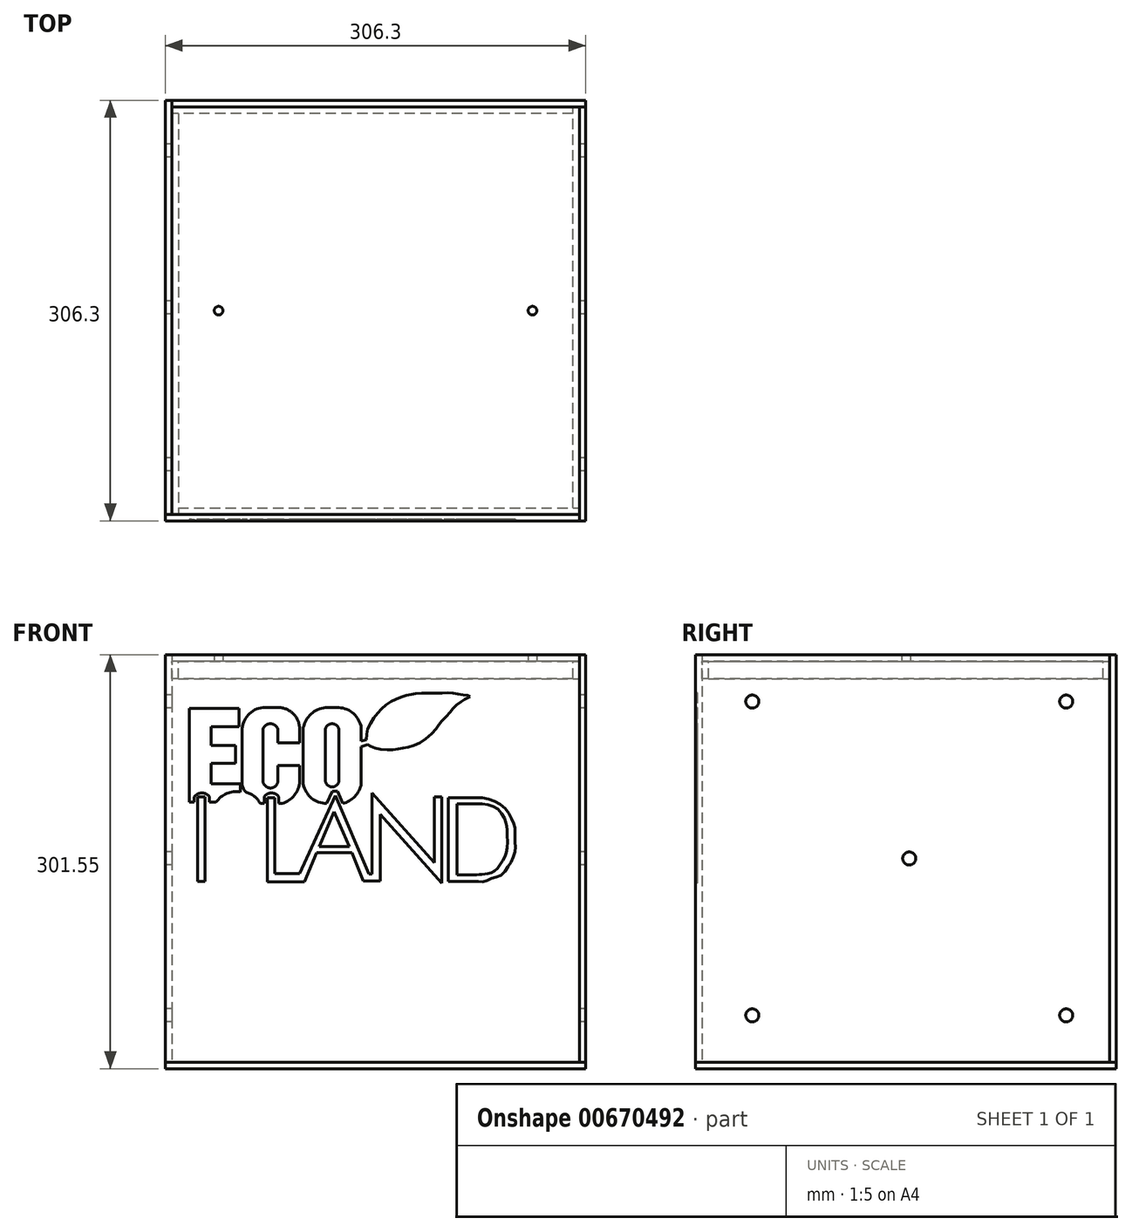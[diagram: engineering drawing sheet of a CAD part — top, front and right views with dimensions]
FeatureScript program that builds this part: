
annotation { "Feature Type Name" : "Feature", "Feature Type Description" : "" }
export const myFeature = defineFeature(function(context is Context, id is Id, definition is map)
    precondition{}
    {
        {
            var Q0;
            Q0=qCreatedBy(makeId("Top.planeOp"),FACE);
            var sketch = newSketch(context, id + "F0", { "sketchPlane" : qUnion([Q0])});
            skLineSegment(sketch, "E0.bottom", {"start": v(-148.4, -148.4) * mm, "end": v(148.4, -148.4) * mm});
            skLineSegment(sketch, "E0.top", {"start": v(-148.4, 148.4) * mm, "end": v(148.4, 148.4) * mm});
            skLineSegment(sketch, "E0.left", {"start": v(-148.4, -148.4) * mm, "end": v(-148.4, 148.4) * mm});
            skLineSegment(sketch, "E0.right", {"start": v(148.4, -148.4) * mm, "end": v(148.4, 148.4) * mm});
            skLineSegment(sketch, "E1.0", {"start": v(-153.15, 153.15) * mm, "end": v(153.15, 153.15) * mm});
            skLineSegment(sketch, "E1.1", {"start": v(-153.15, -153.15) * mm, "end": v(-153.15, 153.15) * mm});
            skLineSegment(sketch, "E1.2", {"start": v(-153.15, -153.15) * mm, "end": v(153.15, -153.15) * mm});
            skLineSegment(sketch, "E1.3", {"start": v(153.15, -153.15) * mm, "end": v(153.15, 153.15) * mm});
            skLineSegment(sketch, "E2", {"start": v(-148.4, 148.4) * mm, "end": v(-148.4, 153.15) * mm});
            skLineSegment(sketch, "E3", {"start": v(-148.4, -148.4) * mm, "end": v(-153.15, -148.4) * mm});
            skLineSegment(sketch, "E4", {"start": v(148.4, -148.4) * mm, "end": v(148.4, -153.15) * mm});
            skLineSegment(sketch, "E5", {"start": v(148.4, 148.4) * mm, "end": v(153.15, 148.4) * mm});
            skSolve(sketch);
        }
        {
            var Q0;
            Q0=makeQuery(id+"F0.imprint","IMPRINT",FACE,{"disambiguationData":[TD([[makeQuery(id+"F0.imprint","IMPRINT",EDGE,{"derivedFrom":sQuery(id+"F0.wireOp",EDGE,"E0.top")}),1.0]])]});
            extrude(context, id + "F1", {"entities" : qUnion([Q0]), "depth" : 296.8 * mm, "offsetDistance" : 25.4 * mm});
        }
        {
            var Q0;
            Q0=makeQuery(id+"F0.imprint","IMPRINT",FACE,{"disambiguationData":[TD([[makeQuery(id+"F0.imprint","IMPRINT",EDGE,{"derivedFrom":sQuery(id+"F0.wireOp",EDGE,"E0.left")}),1.0]])]});
            extrude(context, id + "F2", {"entities" : qUnion([Q0]), "depth" : 296.8 * mm, "offsetDistance" : 25.4 * mm});
        }
        {
            var Q0;
            Q0=makeQuery(id+"F0.imprint","IMPRINT",FACE,{"disambiguationData":[TD([[makeQuery(id+"F0.imprint","IMPRINT",EDGE,{"derivedFrom":sQuery(id+"F0.wireOp",EDGE,"E0.bottom")}),-1.0]])]});
            extrude(context, id + "F3", {"entities" : qUnion([Q0]), "depth" : 296.8 * mm, "offsetDistance" : 25.4 * mm});
        }
        {
            var Q0;
            Q0=makeQuery(id+"F0.imprint","IMPRINT",FACE,{"disambiguationData":[TD([[makeQuery(id+"F0.imprint","IMPRINT",EDGE,{"derivedFrom":sQuery(id+"F0.wireOp",EDGE,"E0.right")}),-1.0]])]});
            extrude(context, id + "F4", {"entities" : qUnion([Q0]), "depth" : 296.8 * mm, "offsetDistance" : 25.4 * mm});
        }
        {
            var Q0;
            Q0=makeQuery(id+"F0.imprint","IMPRINT",FACE,{"disambiguationData":[TD([[makeQuery(id+"F0.imprint","IMPRINT",EDGE,{"derivedFrom":sQuery(id+"F0.wireOp",EDGE,"E0.bottom")}),1.0]])]});
            var Q1;
            Q1=makeQuery(id+"F0.imprint","IMPRINT",FACE,{"disambiguationData":[TD([[makeQuery(id+"F0.imprint","IMPRINT",EDGE,{"derivedFrom":sQuery(id+"F0.wireOp",EDGE,"E0.bottom")}),-1.0]])]});
            var Q2;
            Q2=makeQuery(id+"F0.imprint","IMPRINT",FACE,{"disambiguationData":[TD([[makeQuery(id+"F0.imprint","IMPRINT",EDGE,{"derivedFrom":sQuery(id+"F0.wireOp",EDGE,"E0.left")}),1.0]])]});
            var Q3;
            Q3=makeQuery(id+"F0.imprint","IMPRINT",FACE,{"disambiguationData":[TD([[makeQuery(id+"F0.imprint","IMPRINT",EDGE,{"derivedFrom":sQuery(id+"F0.wireOp",EDGE,"E0.right")}),-1.0]])]});
            var Q4;
            Q4=makeQuery(id+"F0.imprint","IMPRINT",FACE,{"disambiguationData":[TD([[makeQuery(id+"F0.imprint","IMPRINT",EDGE,{"derivedFrom":sQuery(id+"F0.wireOp",EDGE,"E0.top")}),1.0]])]});
            extrude(context, id + "F5", {"entities" : qUnion([Q0, Q1, Q2, Q3, Q4]), "oppositeDirection" : true, "depth" : 4.75 * mm, "offsetDistance" : 25.4 * mm});
        }
        {
            var Q0;
            Q0=makeQuery(id+"F2.opExtrude","CAP_FACE",FACE,{"disambiguationData":[OSD([sQuery(id+"F0.wireOp",EDGE,"E0.left"),sQuery(id+"F0.wireOp",EDGE,"E1.0"),sQuery(id+"F0.wireOp",EDGE,"E1.1"),sQuery(id+"F0.wireOp",EDGE,"E2"),sQuery(id+"F0.wireOp",EDGE,"E3")])],"isStart":false});
            cPlane(context, id + "F6", {"entities" : qUnion([Q0]), "cplaneType" : CPlaneType.OFFSET, "offset" : 4.75 * mm, "oppositeDirection" : true, "width" : 152.4 * mm, "height" : 152.4 * mm});
        }
        {
            var Q0;
            Q0=qCreatedBy(id+"F6.planeOp",FACE);
            var sketch = newSketch(context, id + "F7", { "sketchPlane" : qUnion([Q0])});
            skLineSegment(sketch, "E6.0.0", {"start": v(148.4, 148.4) * mm, "end": v(-148.4, 148.4) * mm});
            skLineSegment(sketch, "E6.0.1", {"start": v(-148.4, 148.4) * mm, "end": v(-148.4, -148.4) * mm});
            skLineSegment(sketch, "E6.0.2", {"start": v(-148.4, -148.4) * mm, "end": v(148.4, -148.4) * mm});
            skLineSegment(sketch, "E6.0.3", {"start": v(148.4, -148.4) * mm, "end": v(148.4, 148.4) * mm});
            skLineSegment(sketch, "E7.0", {"start": v(143.65, 143.65) * mm, "end": v(-143.65, 143.65) * mm});
            skLineSegment(sketch, "E7.1", {"start": v(143.65, -143.65) * mm, "end": v(143.65, 143.65) * mm});
            skLineSegment(sketch, "E7.2", {"start": v(-143.65, -143.65) * mm, "end": v(143.65, -143.65) * mm});
            skLineSegment(sketch, "E7.3", {"start": v(-143.65, 143.65) * mm, "end": v(-143.65, -143.65) * mm});
            skLineSegment(sketch, "E8", {"start": v(-143.65, 143.65) * mm, "end": v(-148.4, 143.65) * mm});
            skLineSegment(sketch, "E9", {"start": v(143.65, 143.65) * mm, "end": v(143.65, 148.4) * mm});
            skLineSegment(sketch, "E10", {"start": v(143.65, -143.65) * mm, "end": v(148.4, -143.65) * mm});
            skLineSegment(sketch, "E11", {"start": v(-143.65, -143.65) * mm, "end": v(-143.65, -148.4) * mm});
            skSolve(sketch);
        }
        {
            var Q0;
            Q0=makeQuery(id+"F7.imprint","IMPRINT",FACE,{"disambiguationData":[TD([[makeQuery(id+"F7.imprint","IMPRINT",EDGE,{"derivedFrom":sQuery(id+"F7.wireOp",EDGE,"E7.0")}),-1.0]])]});
            extrude(context, id + "F8", {"entities" : qUnion([Q0]), "oppositeDirection" : true, "depth" : 12.7 * mm, "offsetDistance" : 25.4 * mm});
        }
        {
            var Q0;
            Q0=makeQuery(id+"F7.imprint","IMPRINT",FACE,{"disambiguationData":[TD([[makeQuery(id+"F7.imprint","IMPRINT",EDGE,{"derivedFrom":sQuery(id+"F7.wireOp",EDGE,"E7.1")}),-1.0]])]});
            extrude(context, id + "F9", {"entities" : qUnion([Q0]), "oppositeDirection" : true, "depth" : 12.7 * mm, "offsetDistance" : 25.4 * mm});
        }
        {
            var Q0;
            Q0=makeQuery(id+"F7.imprint","IMPRINT",FACE,{"disambiguationData":[TD([[makeQuery(id+"F7.imprint","IMPRINT",EDGE,{"derivedFrom":sQuery(id+"F7.wireOp",EDGE,"E7.2")}),-1.0]])]});
            extrude(context, id + "F10", {"entities" : qUnion([Q0]), "oppositeDirection" : true, "depth" : 12.7 * mm, "offsetDistance" : 25.4 * mm});
        }
        {
            var Q0;
            Q0=makeQuery(id+"F7.imprint","IMPRINT",FACE,{"disambiguationData":[TD([[makeQuery(id+"F7.imprint","IMPRINT",EDGE,{"derivedFrom":sQuery(id+"F7.wireOp",EDGE,"E7.3")}),-1.0]])]});
            extrude(context, id + "F11", {"entities" : qUnion([Q0]), "oppositeDirection" : true, "depth" : 12.7 * mm, "offsetDistance" : 25.4 * mm});
        }
        {
            var Q0;
            Q0=qCreatedBy(id+"F6.planeOp",FACE);
            var sketch = newSketch(context, id + "F12", { "sketchPlane" : qUnion([Q0])});
            skLineSegment(sketch, "E12.0.0", {"start": v(148.4, 148.4) * mm, "end": v(-148.4, 148.4) * mm});
            skLineSegment(sketch, "E12.0.1", {"start": v(-148.4, 148.4) * mm, "end": v(-148.4, -148.4) * mm});
            skLineSegment(sketch, "E12.0.2", {"start": v(-148.4, -148.4) * mm, "end": v(148.4, -148.4) * mm});
            skLineSegment(sketch, "E12.0.3", {"start": v(148.4, -148.4) * mm, "end": v(148.4, 148.4) * mm});
            skCircle(sketch, "E13", {"center": v(-114.3, 0) * mm, "radius": 3.18 * mm});
            skCircle(sketch, "E14", {"center": v(114.3, 0) * mm, "radius": 3.18 * mm});
            skSolve(sketch);
        }
        {
            var Q0;
            Q0=makeQuery(id+"F12.imprint","IMPRINT",FACE,{"disambiguationData":[TD([[makeQuery(id+"F12.imprint","IMPRINT",EDGE,{"derivedFrom":sQuery(id+"F12.wireOp",EDGE,"E12.0.0")}),1.0]])]});
            extrude(context, id + "F13", {"entities" : qUnion([Q0]), "depth" : 4.75 * mm, "offsetDistance" : 25.4 * mm});
        }
        {
            var Q0;
            Q0=makeQuery(id+"F2.opExtrude","SWEPT_FACE",FACE,{"disambiguationData":[OSD([sQuery(id+"F0.wireOp",EDGE,"E1.1")])]});
            var sketch = newSketch(context, id + "F14", { "sketchPlane" : qUnion([Q0])});
            skCircle(sketch, "E15", {"center": v(-116.67, 262.7) * mm, "radius": 4.76 * mm});
            skCircle(sketch, "E16", {"center": v(111.93, 262.7) * mm, "radius": 4.76 * mm});
            skCircle(sketch, "E17", {"center": v(-2.37, 148.4) * mm, "radius": 4.76 * mm});
            skCircle(sketch, "E18", {"center": v(-116.67, 34.1) * mm, "radius": 4.76 * mm});
            skCircle(sketch, "E19", {"center": v(111.93, 34.1) * mm, "radius": 4.76 * mm});
            skLineSegment(sketch, "E20", {"start": v(-2.37, 296.8) * mm, "end": v(-2.37, -5.46) * mm, "construction": true});
            skPoint(sketch, "E21.endSnap0", {"position": v(-153.15, 148.4) * mm});
            skLineSegment(sketch, "E22", {"start": v(-153.15, 148.4) * mm, "end": v(153.15, 148.4) * mm, "construction": true});
            skPoint(sketch, "E22.endSnap0", {"position": v(148.4, 148.4) * mm});
            skLineSegment(sketch, "E23.0", {"start": v(-153.15, 262.7) * mm, "end": v(153.15, 262.7) * mm, "construction": true});
            skLineSegment(sketch, "E24.MirrorCS", {"start": v(-153.15, 34.1) * mm, "end": v(153.15, 34.1) * mm, "construction": true});
            skLineSegment(sketch, "E25.0", {"start": v(-116.67, 309.55) * mm, "end": v(-116.67, -5.46) * mm, "construction": true});
            skLineSegment(sketch, "E26.MirrorCS", {"start": v(111.93, 309.55) * mm, "end": v(111.93, -5.46) * mm, "construction": true});
            skSolve(sketch);
        }
        {
            var Q0;
            Q0=makeQuery(id+"F14.imprint","IMPRINT",FACE,{"disambiguationData":[TD([[makeQuery(id+"F14.imprint","IMPRINT",EDGE,{"derivedFrom":sQuery(id+"F14.wireOp",EDGE,"E15")}),1.0]])]});
            var Q1;
            Q1=makeQuery(id+"F14.imprint","IMPRINT",FACE,{"disambiguationData":[TD([[makeQuery(id+"F14.imprint","IMPRINT",EDGE,{"derivedFrom":sQuery(id+"F14.wireOp",EDGE,"E17")}),1.0]])]});
            var Q2;
            Q2=makeQuery(id+"F14.imprint","IMPRINT",FACE,{"disambiguationData":[TD([[makeQuery(id+"F14.imprint","IMPRINT",EDGE,{"derivedFrom":sQuery(id+"F14.wireOp",EDGE,"E16")}),1.0]])]});
            var Q3;
            Q3=makeQuery(id+"F14.imprint","IMPRINT",FACE,{"disambiguationData":[TD([[makeQuery(id+"F14.imprint","IMPRINT",EDGE,{"derivedFrom":sQuery(id+"F14.wireOp",EDGE,"E18")}),1.0]])]});
            var Q4;
            Q4=makeQuery(id+"F14.imprint","IMPRINT",FACE,{"disambiguationData":[TD([[makeQuery(id+"F14.imprint","IMPRINT",EDGE,{"derivedFrom":sQuery(id+"F14.wireOp",EDGE,"E19")}),1.0]])]});
            extrude(context, id + "F15", {"entities" : qUnion([Q0, Q1, Q2, Q3, Q4]), "operationType" : NewBodyOperationType.REMOVE, "endBound" : BoundingType.THROUGH_ALL, "oppositeDirection" : true, "depth" : 25.4 * mm, "offsetDistance" : 25.4 * mm});
        }
        {
            var Q0;
            Q0=makeQuery(id+"F3.opExtrude","SWEPT_FACE",FACE,{"disambiguationData":[OSD([sQuery(id+"F0.wireOp",EDGE,"E1.2")])]});
            var sketch = newSketch(context, id + "F16", { "sketchPlane" : qUnion([Q0])});
            skArc(sketch, "E27", {"start": v(-8.6, 125.15) * mm, "mid": v(-10.23, 126.38) * mm, "end": v(-11.85, 125.15) * mm});
            skLineSegment(sketch, "E28", {"start": v(-8.6, 125.15) * mm, "end": v(-8.6, 112.33) * mm});
            skArc(sketch, "E29", {"start": v(-11.85, 112.33) * mm, "mid": v(-10.23, 111.03) * mm, "end": v(-8.6, 112.33) * mm});
            skLineSegment(sketch, "E30", {"start": v(-11.85, 112.33) * mm, "end": v(-11.85, 125.15) * mm});
            skArc(sketch, "E31", {"start": v(-11.85, 130.29) * mm, "mid": v(-15.35, 128.72) * mm, "end": v(-17.23, 125.38) * mm});
            skLineSegment(sketch, "E32", {"start": v(-8.6, 130.29) * mm, "end": v(-11.85, 130.29) * mm});
            skArc(sketch, "E33", {"start": v(-3.14, 125.38) * mm, "mid": v(-5.01, 128.8) * mm, "end": v(-8.6, 130.29) * mm});
            skLineSegment(sketch, "E34", {"start": v(-3.14, 122.14) * mm, "end": v(-3.14, 125.38) * mm});
            skLineSegment(sketch, "E35", {"start": v(-1.95, 122.5) * mm, "end": v(-3.14, 122.14) * mm});
            skFitSpline(sketch, "E36", {"points": [v(23.25, 132.99) * mm, v(22.72, 133.21) * mm, v(21.03, 133.46) * mm, v(19.07, 133.84) * mm, v(16.72, 133.84) * mm, v(13.07, 133.84) * mm, v(9.94, 133.63) * mm, v(8.25, 133.32) * mm, v(6.05, 132.64) * mm, v(3.77, 131.57) * mm, v(1.55, 129.79) * mm, v(-0.23, 127.6) * mm, v(-1.66, 124.84) * mm, v(-1.95, 122.5) * mm]});
            skFitSpline(sketch, "E37", {"points": [v(-1.57, 121.3) * mm, v(-0.72, 120.85) * mm, v(1.44, 120.18) * mm, v(4.5, 120.06) * mm, v(6.42, 120.36) * mm, v(8.83, 120.8) * mm, v(11.86, 122.23) * mm, v(15.02, 125.15) * mm, v(16, 126.51) * mm, v(17.9, 128.59) * mm, v(19.23, 130.21) * mm, v(20.94, 131.57) * mm, v(22.39, 132.49) * mm, v(23.07, 132.86) * mm, v(23.25, 132.99) * mm]});
            skLineSegment(sketch, "E38", {"start": v(-3.14, 120.8) * mm, "end": v(-1.57, 121.3) * mm});
            skLineSegment(sketch, "E39", {"start": v(-3.14, 111.76) * mm, "end": v(-3.14, 120.8) * mm});
            skArc(sketch, "E40", {"start": v(-7.69, 107) * mm, "mid": v(-4.71, 108.7) * mm, "end": v(-3.14, 111.76) * mm});
            skLineSegment(sketch, "E41", {"start": v(-8.94, 110.02) * mm, "end": v(-7.69, 107) * mm});
            skLineSegment(sketch, "E42", {"start": v(-10.23, 110.02) * mm, "end": v(-8.94, 110.02) * mm});
            skLineSegment(sketch, "E43", {"start": v(-11.52, 107) * mm, "end": v(-10.23, 110.02) * mm});
            skArc(sketch, "E44", {"start": v(-17.23, 111.76) * mm, "mid": v(-15.25, 108.32) * mm, "end": v(-11.52, 107) * mm});
            skLineSegment(sketch, "E45", {"start": v(-17.23, 125.38) * mm, "end": v(-17.23, 111.76) * mm});
            skFitSpline(sketch, "E46", {"points": [v(26.21, 106.92) * mm, v(30.03, 105.58) * mm, v(31.97, 102.38) * mm, v(32.23, 100.6) * mm, v(32.23, 96) * mm, v(31.5, 93.66) * mm, v(29.77, 91.13) * mm, v(28.35, 90.2) * mm, v(26.9, 89.88) * mm, v(25.75, 89.77) * mm, v(24.83, 89.7) * mm]});
            skLineSegment(sketch, "E47", {"start": v(24.83, 89.7) * mm, "end": v(20.09, 89.7) * mm});
            skLineSegment(sketch, "E48", {"start": v(20.09, 89.7) * mm, "end": v(20.09, 106.92) * mm});
            skLineSegment(sketch, "E49", {"start": v(20.09, 106.92) * mm, "end": v(26.21, 106.92) * mm});
            skLineSegment(sketch, "E50", {"start": v(26.2, 108.36) * mm, "end": v(18.02, 108.36) * mm});
            skFitSpline(sketch, "E51", {"points": [v(25.26, 88.07) * mm, v(26.9, 88.07) * mm, v(28.65, 88.87) * mm, v(30.52, 89.42) * mm, v(32.23, 91.3) * mm, v(33.5, 93.37) * mm, v(34.2, 95.62) * mm, v(34.2, 97.62) * mm, v(34.2, 100.15) * mm, v(34.2, 101.2) * mm, v(33.45, 102.97) * mm, v(32.11, 105.38) * mm, v(29.35, 107.47) * mm, v(26.2, 108.36) * mm]});
            skLineSegment(sketch, "E52", {"start": v(18.02, 88.07) * mm, "end": v(25.26, 88.07) * mm});
            skLineSegment(sketch, "E53", {"start": v(18.02, 108.36) * mm, "end": v(18.02, 88.07) * mm});
            skLineSegment(sketch, "E54", {"start": v(-32.88, 130.05) * mm, "end": v(-44.89, 130.05) * mm});
            skLineSegment(sketch, "E55", {"start": v(-32.88, 125.6) * mm, "end": v(-32.88, 130.05) * mm});
            skLineSegment(sketch, "E56", {"start": v(-39.55, 125.6) * mm, "end": v(-32.88, 125.6) * mm});
            skLineSegment(sketch, "E57", {"start": v(-39.55, 121.07) * mm, "end": v(-39.55, 125.6) * mm});
            skLineSegment(sketch, "E58", {"start": v(-33.63, 121.07) * mm, "end": v(-39.55, 121.07) * mm});
            skLineSegment(sketch, "E59", {"start": v(-33.63, 116.75) * mm, "end": v(-33.63, 121.07) * mm});
            skLineSegment(sketch, "E60", {"start": v(-39.55, 116.75) * mm, "end": v(-33.63, 116.75) * mm});
            skLineSegment(sketch, "E61", {"start": v(-39.55, 111.76) * mm, "end": v(-39.55, 116.75) * mm});
            skLineSegment(sketch, "E62", {"start": v(-32.5, 111.76) * mm, "end": v(-39.55, 111.76) * mm});
            skLineSegment(sketch, "E63", {"start": v(-32.5, 109.78) * mm, "end": v(-32.5, 111.76) * mm});
            skArc(sketch, "E64", {"start": v(-32.5, 109.78) * mm, "mid": v(-35.8, 109.4) * mm, "end": v(-38.4, 107.34) * mm});
            skLineSegment(sketch, "E65", {"start": v(-39.99, 107.34) * mm, "end": v(-38.4, 107.34) * mm});
            skLineSegment(sketch, "E66", {"start": v(-39.99, 108.6) * mm, "end": v(-39.99, 107.34) * mm});
            skArc(sketch, "E67", {"start": v(-39.99, 108.6) * mm, "mid": v(-41.84, 109.55) * mm, "end": v(-43.7, 108.6) * mm});
            skLineSegment(sketch, "E68", {"start": v(-43.7, 107.34) * mm, "end": v(-43.7, 108.6) * mm});
            skLineSegment(sketch, "E69", {"start": v(-44.89, 107.34) * mm, "end": v(-43.7, 107.34) * mm});
            skLineSegment(sketch, "E70", {"start": v(-44.89, 130.05) * mm, "end": v(-44.89, 107.34) * mm});
            skLineSegment(sketch, "E71", {"start": v(-9.73, 105) * mm, "end": v(-6.08, 96.57) * mm});
            skLineSegment(sketch, "E72", {"start": v(-6.08, 96.57) * mm, "end": v(-13.34, 96.57) * mm});
            skLineSegment(sketch, "E73", {"start": v(-13.34, 96.57) * mm, "end": v(-9.73, 105) * mm});
            skLineSegment(sketch, "E74", {"start": v(-24.14, 89.97) * mm, "end": v(-24.14, 108.36) * mm});
            skLineSegment(sketch, "E75", {"start": v(-18.16, 89.97) * mm, "end": v(-24.14, 89.97) * mm});
            skLineSegment(sketch, "E76", {"start": v(-9.45, 108.96) * mm, "end": v(-18.16, 89.97) * mm});
            skLineSegment(sketch, "E77", {"start": v(-1.29, 89.88) * mm, "end": v(-9.45, 108.96) * mm});
            skLineSegment(sketch, "E78", {"start": v(-2.71, 88.13) * mm, "end": v(-0.51, 88.13) * mm});
            skLineSegment(sketch, "E79", {"start": v(-5.47, 95.03) * mm, "end": v(-2.71, 88.13) * mm});
            skLineSegment(sketch, "E80", {"start": v(-14, 95.03) * mm, "end": v(-5.47, 95.03) * mm});
            skLineSegment(sketch, "E81", {"start": v(-17, 88.02) * mm, "end": v(-14, 95.03) * mm});
            skLineSegment(sketch, "E82", {"start": v(-25.93, 88.02) * mm, "end": v(-17, 88.02) * mm});
            skLineSegment(sketch, "E83", {"start": v(-25.93, 108.36) * mm, "end": v(-25.93, 88.02) * mm});
            skLineSegment(sketch, "E84", {"start": v(-24.14, 108.36) * mm, "end": v(-25.93, 108.36) * mm});
            skLineSegment(sketch, "E85", {"start": v(-0.51, 109.55) * mm, "end": v(-0.51, 89.88) * mm});
            skLineSegment(sketch, "E86", {"start": v(14.56, 92.6) * mm, "end": v(-0.51, 109.55) * mm});
            skLineSegment(sketch, "E87", {"start": v(14.56, 108.6) * mm, "end": v(14.56, 92.6) * mm});
            skLineSegment(sketch, "E88", {"start": v(16.34, 108.6) * mm, "end": v(14.56, 108.6) * mm});
            skLineSegment(sketch, "E89", {"start": v(16.34, 87.62) * mm, "end": v(16.34, 108.6) * mm});
            skLineSegment(sketch, "E90", {"start": v(1.44, 104.38) * mm, "end": v(16.34, 87.62) * mm});
            skLineSegment(sketch, "E91", {"start": v(1.44, 88.02) * mm, "end": v(1.44, 104.38) * mm});
            skLineSegment(sketch, "E92", {"start": v(-0.51, 88.13) * mm, "end": v(1.45, 88.13) * mm});
            skFitSpline(sketch, "E93", {"points": [v(-39.55, 91.54) * mm, v(-39.2, 90.9) * mm, v(-38.58, 89.97) * mm, v(-37.66, 88.87) * mm, v(-36.07, 88.02) * mm, v(-34.9, 87.63) * mm, v(-32.5, 87.63) * mm, v(-32.5, 87.63) * mm, v(-31.22, 87.9) * mm, v(-29.93, 88.35) * mm, v(-28.75, 89.47) * mm, v(-27.9, 90.5) * mm, v(-27.3, 91.92) * mm, v(-27.3, 93.66) * mm, v(-27.57, 95.15) * mm, v(-28.06, 96.57) * mm, v(-29.42, 97.98) * mm, v(-31.29, 99.33) * mm, v(-32.88, 100.15) * mm, v(-34.4, 100.92) * mm, v(-35.8, 102.21) * mm, v(-36.4, 102.87) * mm, v(-36.59, 103.98) * mm, v(-36.55, 105.37) * mm, v(-36.4, 105.91) * mm, v(-35.7, 106.64) * mm, v(-34.9, 107.1) * mm, v(-34.29, 107.44) * mm, v(-33.22, 107.44) * mm, v(-32.37, 107.44) * mm, v(-31.83, 107.22) * mm, v(-30.85, 106.78) * mm, v(-29.72, 105.55) * mm]});
            skLineSegment(sketch, "E94", {"start": v(-38.07, 92.49) * mm, "end": v(-39.55, 91.54) * mm});
            skFitSpline(sketch, "E95", {"points": [v(-28.36, 106.37) * mm, v(-29.87, 108.07) * mm, v(-30.97, 108.64) * mm, v(-32.1, 108.86) * mm, v(-33.44, 108.96) * mm, v(-34.87, 108.8) * mm, v(-36.18, 108.26) * mm, v(-36.9, 107.68) * mm, v(-37.68, 107) * mm, v(-38.2, 105.96) * mm, v(-38.5, 105.24) * mm, v(-38.61, 104.37) * mm, v(-38.52, 102.97) * mm, v(-38.11, 101.8) * mm, v(-37.34, 101.08) * mm, v(-35.38, 99.55) * mm, v(-33.13, 98.33) * mm, v(-31.29, 97.13) * mm, v(-29.93, 96.01) * mm, v(-29.35, 94.95) * mm, v(-29.09, 93.5) * mm, v(-29.09, 92.32) * mm, v(-29.61, 91.08) * mm, v(-30.62, 90) * mm, v(-31.67, 89.43) * mm, v(-32.5, 89.21) * mm, v(-33.7, 89.21) * mm, v(-34.29, 89.21) * mm, v(-35.8, 89.73) * mm, v(-36.55, 90.2) * mm, v(-37.16, 90.97) * mm, v(-37.66, 91.68) * mm, v(-38.07, 92.49) * mm]});
            skLineSegment(sketch, "E96", {"start": v(-29.72, 105.55) * mm, "end": v(-28.36, 106.37) * mm});
            skLineSegment(sketch, "E97", {"start": v(-41.05, 88.06) * mm, "end": v(-41.05, 108.6) * mm});
            skLineSegment(sketch, "E98", {"start": v(-42.84, 88.06) * mm, "end": v(-41.05, 88.06) * mm});
            skLineSegment(sketch, "E99", {"start": v(-42.84, 108.6) * mm, "end": v(-42.84, 88.06) * mm});
            skLineSegment(sketch, "E100", {"start": v(-41.05, 108.6) * mm, "end": v(-42.84, 108.6) * mm});
            skLineSegment(sketch, "E101", {"start": v(51.59, 95.86) * mm, "end": v(51.59, 88.87) * mm});
            skLineSegment(sketch, "E102", {"start": v(52.13, 95.86) * mm, "end": v(51.59, 95.86) * mm});
            skLineSegment(sketch, "E103", {"start": v(52.13, 89.32) * mm, "end": v(52.13, 95.86) * mm});
            skLineSegment(sketch, "E104", {"start": v(54.69, 89.32) * mm, "end": v(52.13, 89.32) * mm});
            skLineSegment(sketch, "E105", {"start": v(54.69, 88.87) * mm, "end": v(54.69, 89.32) * mm});
            skLineSegment(sketch, "E106", {"start": v(51.59, 88.87) * mm, "end": v(54.69, 88.87) * mm});
            skLineSegment(sketch, "E107", {"start": v(48.62, 89.32) * mm, "end": v(48.62, 95.86) * mm});
            skLineSegment(sketch, "E108", {"start": v(51.18, 89.32) * mm, "end": v(48.62, 89.32) * mm});
            skLineSegment(sketch, "E109", {"start": v(51.18, 88.87) * mm, "end": v(51.18, 89.32) * mm});
            skLineSegment(sketch, "E110", {"start": v(48.08, 88.87) * mm, "end": v(51.18, 88.87) * mm});
            skLineSegment(sketch, "E111", {"start": v(48.08, 95.86) * mm, "end": v(48.08, 88.87) * mm});
            skLineSegment(sketch, "E112", {"start": v(48.62, 95.86) * mm, "end": v(48.08, 95.86) * mm});
            skLineSegment(sketch, "E113", {"start": v(61.15, 94.65) * mm, "end": v(61.15, 95.73) * mm});
            skArc(sketch, "E114", {"start": v(61.15, 94.65) * mm, "mid": v(55.43, 92.49) * mm, "end": v(61.15, 90.32) * mm});
            skLineSegment(sketch, "E115", {"start": v(61.15, 89.24) * mm, "end": v(61.15, 90.32) * mm});
            skArc(sketch, "E116", {"start": v(61.15, 95.73) * mm, "mid": v(54.63, 92.49) * mm, "end": v(61.15, 89.24) * mm});
            skFitSpline(sketch, "E117", {"points": [v(33.37, 91.54) * mm, v(33.72, 90.9) * mm, v(34.34, 89.97) * mm, v(35.26, 88.87) * mm, v(36.85, 88.02) * mm, v(38.02, 87.63) * mm, v(40.41, 87.63) * mm, v(40.41, 87.63) * mm, v(41.7, 87.9) * mm, v(43, 88.35) * mm, v(44.17, 89.47) * mm, v(45.01, 90.5) * mm, v(45.62, 91.92) * mm, v(45.62, 93.66) * mm, v(45.35, 95.15) * mm, v(44.86, 96.57) * mm, v(43.5, 97.98) * mm, v(41.63, 99.33) * mm, v(40.04, 100.15) * mm, v(38.52, 100.92) * mm, v(37.12, 102.21) * mm, v(36.52, 102.87) * mm, v(36.33, 103.98) * mm, v(36.37, 105.37) * mm, v(36.52, 105.91) * mm, v(37.22, 106.64) * mm, v(38.02, 107.1) * mm, v(38.63, 107.44) * mm, v(39.7, 107.44) * mm, v(40.55, 107.44) * mm, v(41.1, 107.22) * mm, v(42.07, 106.78) * mm, v(43.2, 105.55) * mm]});
            skLineSegment(sketch, "E118", {"start": v(34.85, 92.49) * mm, "end": v(33.37, 91.54) * mm});
            skFitSpline(sketch, "E119", {"points": [v(44.56, 106.37) * mm, v(43.05, 108.07) * mm, v(41.94, 108.64) * mm, v(40.82, 108.86) * mm, v(39.48, 108.96) * mm, v(38.05, 108.8) * mm, v(36.74, 108.26) * mm, v(36.03, 107.68) * mm, v(35.24, 107) * mm, v(34.72, 105.96) * mm, v(34.41, 105.24) * mm, v(34.3, 104.37) * mm, v(34.4, 102.97) * mm, v(34.8, 101.8) * mm, v(35.57, 101.08) * mm, v(37.54, 99.55) * mm, v(39.79, 98.33) * mm, v(41.63, 97.13) * mm, v(43, 96.01) * mm, v(43.57, 94.95) * mm, v(43.83, 93.5) * mm, v(43.83, 92.32) * mm, v(43.3, 91.08) * mm, v(42.3, 90) * mm, v(41.24, 89.43) * mm, v(40.41, 89.21) * mm, v(39.23, 89.21) * mm, v(38.63, 89.21) * mm, v(37.12, 89.73) * mm, v(36.37, 90.2) * mm, v(35.76, 90.97) * mm, v(35.26, 91.68) * mm, v(34.85, 92.49) * mm]});
            skLineSegment(sketch, "E120", {"start": v(43.2, 105.55) * mm, "end": v(44.56, 106.37) * mm});
            skArc(sketch, "E121", {"start": v(-26.97, 130.29) * mm, "mid": v(-30.62, 128.5) * mm, "end": v(-32.1, 124.7) * mm});
            skLineSegment(sketch, "E122", {"start": v(-23.43, 130.29) * mm, "end": v(-26.97, 130.29) * mm});
            skArc(sketch, "E123", {"start": v(-18.12, 125.13) * mm, "mid": v(-19.69, 128.83) * mm, "end": v(-23.43, 130.29) * mm});
            skLineSegment(sketch, "E124", {"start": v(-18.12, 121.69) * mm, "end": v(-18.12, 125.13) * mm});
            skLineSegment(sketch, "E125", {"start": v(-23.43, 121.69) * mm, "end": v(-18.12, 121.69) * mm});
            skLineSegment(sketch, "E126", {"start": v(-23.43, 125.15) * mm, "end": v(-23.43, 121.69) * mm});
            skArc(sketch, "E127", {"start": v(-23.43, 125.15) * mm, "mid": v(-25.2, 126.36) * mm, "end": v(-26.97, 125.15) * mm});
            skLineSegment(sketch, "E128", {"start": v(-26.97, 112.1) * mm, "end": v(-26.97, 125.15) * mm});
            skArc(sketch, "E129", {"start": v(-26.97, 112.1) * mm, "mid": v(-25.2, 110.76) * mm, "end": v(-23.43, 112.1) * mm});
            skLineSegment(sketch, "E130", {"start": v(-23.43, 116.21) * mm, "end": v(-23.43, 112.1) * mm});
            skLineSegment(sketch, "E131", {"start": v(-18.12, 116.21) * mm, "end": v(-23.43, 116.21) * mm});
            skLineSegment(sketch, "E132", {"start": v(-18.12, 112.33) * mm, "end": v(-18.12, 116.21) * mm});
            skArc(sketch, "E133", {"start": v(-22.38, 107) * mm, "mid": v(-19.4, 109) * mm, "end": v(-18.12, 112.33) * mm});
            skLineSegment(sketch, "E134", {"start": v(-23.2, 107) * mm, "end": v(-22.38, 107) * mm});
            skLineSegment(sketch, "E135", {"start": v(-23.2, 108.6) * mm, "end": v(-23.2, 107) * mm});
            skArc(sketch, "E136", {"start": v(-23.2, 108.6) * mm, "mid": v(-24.96, 109.55) * mm, "end": v(-26.73, 108.6) * mm});
            skLineSegment(sketch, "E137", {"start": v(-26.73, 107) * mm, "end": v(-26.73, 108.6) * mm});
            skLineSegment(sketch, "E138", {"start": v(-27.68, 107) * mm, "end": v(-26.73, 107) * mm});
            skArc(sketch, "E139", {"start": v(-27.68, 107) * mm, "mid": v(-29.14, 108.75) * mm, "end": v(-31.18, 109.78) * mm});
            skArc(sketch, "E140", {"start": v(-32.1, 112.6) * mm, "mid": v(-31.95, 111.1) * mm, "end": v(-31.18, 109.78) * mm});
            skLineSegment(sketch, "E141", {"start": v(-32.1, 124.7) * mm, "end": v(-32.1, 112.6) * mm});
            skLineSegment(sketch, "E142", {"start": v(-1.29, 89.88) * mm, "end": v(-0.51, 89.88) * mm});
            skSolve(sketch);
        }
        {
            var Q0;
            Q0=makeQuery(id+"F16.imprint","IMPRINT",FACE,{"disambiguationData":[TD([[makeQuery(id+"F16.imprint","IMPRINT",EDGE,{"derivedFrom":sQuery(id+"F16.wireOp",EDGE,"E54")}),1.0]])]});
            var Q1;
            Q1=makeQuery(id+"F16.imprint","IMPRINT",FACE,{"disambiguationData":[TD([[makeQuery(id+"F16.imprint","IMPRINT",EDGE,{"derivedFrom":sQuery(id+"F16.wireOp",EDGE,"E121")}),1.0]])]});
            var Q2;
            Q2=makeQuery(id+"F16.imprint","IMPRINT",FACE,{"disambiguationData":[TD([[makeQuery(id+"F16.imprint","IMPRINT",EDGE,{"derivedFrom":sQuery(id+"F16.wireOp",EDGE,"E27")}),-1.0]])]});
            var Q3;
            Q3=makeQuery(id+"F16.imprint","IMPRINT",FACE,{"disambiguationData":[TD([[makeQuery(id+"F16.imprint","IMPRINT",EDGE,{"derivedFrom":sQuery(id+"F16.wireOp",EDGE,"E97")}),1.0]])]});
            var Q4;
            Q4=makeQuery(id+"F16.imprint","IMPRINT",FACE,{"disambiguationData":[TD([[makeQuery(id+"F16.imprint","IMPRINT",EDGE,{"derivedFrom":sQuery(id+"F16.wireOp",EDGE,"E93")}),1.0]])]});
            var Q5;
            Q5=makeQuery(id+"F16.imprint","IMPRINT",FACE,{"disambiguationData":[TD([[makeQuery(id+"F16.imprint","IMPRINT",EDGE,{"derivedFrom":sQuery(id+"F16.wireOp",EDGE,"E85")}),1.0]])]});
            var Q6;
            Q6=makeQuery(id+"F16.imprint","IMPRINT",FACE,{"disambiguationData":[TD([[makeQuery(id+"F16.imprint","IMPRINT",EDGE,{"derivedFrom":sQuery(id+"F16.wireOp",EDGE,"E46")}),1.0]])]});
            var Q7;
            Q7=makeQuery(id+"F16.imprint","IMPRINT",FACE,{"disambiguationData":[TD([[makeQuery(id+"F16.imprint","IMPRINT",EDGE,{"derivedFrom":sQuery(id+"F16.wireOp",EDGE,"E117")}),1.0]])]});
            var Q8;
            Q8=makeQuery(id+"F16.imprint","IMPRINT",FACE,{"disambiguationData":[TD([[makeQuery(id+"F16.imprint","IMPRINT",EDGE,{"derivedFrom":sQuery(id+"F16.wireOp",EDGE,"eeda3bce-2852-4320-804d-5f9b85010774")}),1.0]])]});
            extrude(context, id + "F17", {"entities" : qUnion([Q0, Q1, Q2, Q3, Q4, Q5, Q6, Q7, Q8]), "oppositeDirection" : true, "depth" : 0.38 * mm, "offsetDistance" : 25.4 * mm});
        }
        {
            var Q0;
            Q0=makeQuery(id+"F17.opExtrude","SWEPT_BODY",BODY,{"disambiguationData":[OSD([sQuery(id+"F16.wireOp",EDGE,"E27"),sQuery(id+"F16.wireOp",EDGE,"E28"),sQuery(id+"F16.wireOp",EDGE,"E29"),sQuery(id+"F16.wireOp",EDGE,"E30"),sQuery(id+"F16.wireOp",EDGE,"E31"),sQuery(id+"F16.wireOp",EDGE,"E32"),sQuery(id+"F16.wireOp",EDGE,"E33"),sQuery(id+"F16.wireOp",EDGE,"E34"),sQuery(id+"F16.wireOp",EDGE,"E35"),sQuery(id+"F16.wireOp",EDGE,"E36"),sQuery(id+"F16.wireOp",EDGE,"E37"),sQuery(id+"F16.wireOp",EDGE,"E38"),sQuery(id+"F16.wireOp",EDGE,"E39"),sQuery(id+"F16.wireOp",EDGE,"E40"),sQuery(id+"F16.wireOp",EDGE,"E41"),sQuery(id+"F16.wireOp",EDGE,"E42"),sQuery(id+"F16.wireOp",EDGE,"E43"),sQuery(id+"F16.wireOp",EDGE,"E44"),sQuery(id+"F16.wireOp",EDGE,"E45")])]});
            var Q1;
            Q1=makeQuery(id+"F17.opExtrude","SWEPT_BODY",BODY,{"disambiguationData":[OSD([sQuery(id+"F16.wireOp",EDGE,"E46"),sQuery(id+"F16.wireOp",EDGE,"E47"),sQuery(id+"F16.wireOp",EDGE,"E48"),sQuery(id+"F16.wireOp",EDGE,"E49"),sQuery(id+"F16.wireOp",EDGE,"E50"),sQuery(id+"F16.wireOp",EDGE,"E51"),sQuery(id+"F16.wireOp",EDGE,"E52"),sQuery(id+"F16.wireOp",EDGE,"E53")])]});
            var Q2;
            Q2=makeQuery(id+"F17.opExtrude","SWEPT_BODY",BODY,{"disambiguationData":[OSD([sQuery(id+"F16.wireOp",EDGE,"E54"),sQuery(id+"F16.wireOp",EDGE,"E55"),sQuery(id+"F16.wireOp",EDGE,"E56"),sQuery(id+"F16.wireOp",EDGE,"E57"),sQuery(id+"F16.wireOp",EDGE,"E58"),sQuery(id+"F16.wireOp",EDGE,"E59"),sQuery(id+"F16.wireOp",EDGE,"E60"),sQuery(id+"F16.wireOp",EDGE,"E61"),sQuery(id+"F16.wireOp",EDGE,"E62"),sQuery(id+"F16.wireOp",EDGE,"E63"),sQuery(id+"F16.wireOp",EDGE,"E64"),sQuery(id+"F16.wireOp",EDGE,"E65"),sQuery(id+"F16.wireOp",EDGE,"E66"),sQuery(id+"F16.wireOp",EDGE,"E67"),sQuery(id+"F16.wireOp",EDGE,"E68"),sQuery(id+"F16.wireOp",EDGE,"E69"),sQuery(id+"F16.wireOp",EDGE,"E70")])]});
            var Q3;
            Q3=makeQuery(id+"F17.opExtrude","SWEPT_BODY",BODY,{"disambiguationData":[OSD([sQuery(id+"F16.wireOp",EDGE,"E71"),sQuery(id+"F16.wireOp",EDGE,"E72"),sQuery(id+"F16.wireOp",EDGE,"E73"),sQuery(id+"F16.wireOp",EDGE,"E74"),sQuery(id+"F16.wireOp",EDGE,"E75"),sQuery(id+"F16.wireOp",EDGE,"E76"),sQuery(id+"F16.wireOp",EDGE,"E77"),sQuery(id+"F16.wireOp",EDGE,"E78"),sQuery(id+"F16.wireOp",EDGE,"E79"),sQuery(id+"F16.wireOp",EDGE,"E80"),sQuery(id+"F16.wireOp",EDGE,"E81"),sQuery(id+"F16.wireOp",EDGE,"E82"),sQuery(id+"F16.wireOp",EDGE,"E83"),sQuery(id+"F16.wireOp",EDGE,"E84"),sQuery(id+"F16.wireOp",EDGE,"E85"),sQuery(id+"F16.wireOp",EDGE,"E86"),sQuery(id+"F16.wireOp",EDGE,"E87"),sQuery(id+"F16.wireOp",EDGE,"E88"),sQuery(id+"F16.wireOp",EDGE,"E89"),sQuery(id+"F16.wireOp",EDGE,"E90"),sQuery(id+"F16.wireOp",EDGE,"E91"),sQuery(id+"F16.wireOp",EDGE,"E92"),sQuery(id+"F16.wireOp",EDGE,"E142")])]});
            var Q4;
            Q4=makeQuery(id+"F17.opExtrude","SWEPT_BODY",BODY,{"disambiguationData":[OSD([sQuery(id+"F16.wireOp",EDGE,"E93"),sQuery(id+"F16.wireOp",EDGE,"E94"),sQuery(id+"F16.wireOp",EDGE,"E95"),sQuery(id+"F16.wireOp",EDGE,"E96")])]});
            var Q5;
            Q5=makeQuery(id+"F17.opExtrude","SWEPT_BODY",BODY,{"disambiguationData":[OSD([sQuery(id+"F16.wireOp",EDGE,"E97"),sQuery(id+"F16.wireOp",EDGE,"E98"),sQuery(id+"F16.wireOp",EDGE,"E99"),sQuery(id+"F16.wireOp",EDGE,"E100")])]});
            var Q6;
            Q6=makeQuery(id+"F17.opExtrude","SWEPT_BODY",BODY,{"disambiguationData":[OSD([sQuery(id+"F16.wireOp",EDGE,"E117"),sQuery(id+"F16.wireOp",EDGE,"E118"),sQuery(id+"F16.wireOp",EDGE,"E119"),sQuery(id+"F16.wireOp",EDGE,"E120")])]});
            var Q7;
            Q7=makeQuery(id+"F17.opExtrude","SWEPT_BODY",BODY,{"disambiguationData":[OSD([sQuery(id+"F16.wireOp",EDGE,"E121"),sQuery(id+"F16.wireOp",EDGE,"E122"),sQuery(id+"F16.wireOp",EDGE,"E123"),sQuery(id+"F16.wireOp",EDGE,"E124"),sQuery(id+"F16.wireOp",EDGE,"E125"),sQuery(id+"F16.wireOp",EDGE,"E126"),sQuery(id+"F16.wireOp",EDGE,"E127"),sQuery(id+"F16.wireOp",EDGE,"E128"),sQuery(id+"F16.wireOp",EDGE,"E129"),sQuery(id+"F16.wireOp",EDGE,"E130"),sQuery(id+"F16.wireOp",EDGE,"E131"),sQuery(id+"F16.wireOp",EDGE,"E132"),sQuery(id+"F16.wireOp",EDGE,"E133"),sQuery(id+"F16.wireOp",EDGE,"E134"),sQuery(id+"F16.wireOp",EDGE,"E135"),sQuery(id+"F16.wireOp",EDGE,"E136"),sQuery(id+"F16.wireOp",EDGE,"E137"),sQuery(id+"F16.wireOp",EDGE,"E138"),sQuery(id+"F16.wireOp",EDGE,"E139"),sQuery(id+"F16.wireOp",EDGE,"E140"),sQuery(id+"F16.wireOp",EDGE,"E141")])]});
            var Q8;
            Q8=makeQuery(id+"F17.opExtrude","CAP_VERTEX",VERTEX,{"disambiguationData":[OSD([sQuery(id+"F16.wireOp",EDGE,"E78"),sQuery(id+"F16.wireOp",EDGE,"E79")])],"isStart":true});
            transform(context, id + "F18", {"entities" : qUnion([Q0, Q1, Q2, Q3, Q4, Q5, Q6, Q7]), "transformType" : TransformType.SCALE_UNIFORMLY, "scale" : 3, "scalePoint" : qUnion([Q8]), "makeCopy" : false});
        }
        {
            var Q0;
            Q0=makeQuery(id+"F17.opExtrude","SWEPT_BODY",BODY,{"disambiguationData":[OSD([sQuery(id+"F16.wireOp",EDGE,"E27"),sQuery(id+"F16.wireOp",EDGE,"E28"),sQuery(id+"F16.wireOp",EDGE,"E29"),sQuery(id+"F16.wireOp",EDGE,"E30"),sQuery(id+"F16.wireOp",EDGE,"E31"),sQuery(id+"F16.wireOp",EDGE,"E32"),sQuery(id+"F16.wireOp",EDGE,"E33"),sQuery(id+"F16.wireOp",EDGE,"E34"),sQuery(id+"F16.wireOp",EDGE,"E35"),sQuery(id+"F16.wireOp",EDGE,"E36"),sQuery(id+"F16.wireOp",EDGE,"E37"),sQuery(id+"F16.wireOp",EDGE,"E38"),sQuery(id+"F16.wireOp",EDGE,"E39"),sQuery(id+"F16.wireOp",EDGE,"E40"),sQuery(id+"F16.wireOp",EDGE,"E41"),sQuery(id+"F16.wireOp",EDGE,"E42"),sQuery(id+"F16.wireOp",EDGE,"E43"),sQuery(id+"F16.wireOp",EDGE,"E44"),sQuery(id+"F16.wireOp",EDGE,"E45")])]});
            var Q1;
            Q1=makeQuery(id+"F17.opExtrude","SWEPT_BODY",BODY,{"disambiguationData":[OSD([sQuery(id+"F16.wireOp",EDGE,"E46"),sQuery(id+"F16.wireOp",EDGE,"E47"),sQuery(id+"F16.wireOp",EDGE,"E48"),sQuery(id+"F16.wireOp",EDGE,"E49"),sQuery(id+"F16.wireOp",EDGE,"E50"),sQuery(id+"F16.wireOp",EDGE,"E51"),sQuery(id+"F16.wireOp",EDGE,"E52"),sQuery(id+"F16.wireOp",EDGE,"E53")])]});
            var Q2;
            Q2=makeQuery(id+"F17.opExtrude","SWEPT_BODY",BODY,{"disambiguationData":[OSD([sQuery(id+"F16.wireOp",EDGE,"E54"),sQuery(id+"F16.wireOp",EDGE,"E55"),sQuery(id+"F16.wireOp",EDGE,"E56"),sQuery(id+"F16.wireOp",EDGE,"E57"),sQuery(id+"F16.wireOp",EDGE,"E58"),sQuery(id+"F16.wireOp",EDGE,"E59"),sQuery(id+"F16.wireOp",EDGE,"E60"),sQuery(id+"F16.wireOp",EDGE,"E61"),sQuery(id+"F16.wireOp",EDGE,"E62"),sQuery(id+"F16.wireOp",EDGE,"E63"),sQuery(id+"F16.wireOp",EDGE,"E64"),sQuery(id+"F16.wireOp",EDGE,"E65"),sQuery(id+"F16.wireOp",EDGE,"E66"),sQuery(id+"F16.wireOp",EDGE,"E67"),sQuery(id+"F16.wireOp",EDGE,"E68"),sQuery(id+"F16.wireOp",EDGE,"E69"),sQuery(id+"F16.wireOp",EDGE,"E70")])]});
            var Q3;
            Q3=makeQuery(id+"F17.opExtrude","SWEPT_BODY",BODY,{"disambiguationData":[OSD([sQuery(id+"F16.wireOp",EDGE,"E71"),sQuery(id+"F16.wireOp",EDGE,"E72"),sQuery(id+"F16.wireOp",EDGE,"E73"),sQuery(id+"F16.wireOp",EDGE,"E74"),sQuery(id+"F16.wireOp",EDGE,"E75"),sQuery(id+"F16.wireOp",EDGE,"E76"),sQuery(id+"F16.wireOp",EDGE,"E77"),sQuery(id+"F16.wireOp",EDGE,"E78"),sQuery(id+"F16.wireOp",EDGE,"E79"),sQuery(id+"F16.wireOp",EDGE,"E80"),sQuery(id+"F16.wireOp",EDGE,"E81"),sQuery(id+"F16.wireOp",EDGE,"E82"),sQuery(id+"F16.wireOp",EDGE,"E83"),sQuery(id+"F16.wireOp",EDGE,"E84"),sQuery(id+"F16.wireOp",EDGE,"E85"),sQuery(id+"F16.wireOp",EDGE,"E86"),sQuery(id+"F16.wireOp",EDGE,"E87"),sQuery(id+"F16.wireOp",EDGE,"E88"),sQuery(id+"F16.wireOp",EDGE,"E89"),sQuery(id+"F16.wireOp",EDGE,"E90"),sQuery(id+"F16.wireOp",EDGE,"E91"),sQuery(id+"F16.wireOp",EDGE,"E92"),sQuery(id+"F16.wireOp",EDGE,"E142")])]});
            var Q4;
            Q4=makeQuery(id+"F17.opExtrude","SWEPT_BODY",BODY,{"disambiguationData":[OSD([sQuery(id+"F16.wireOp",EDGE,"E93"),sQuery(id+"F16.wireOp",EDGE,"E94"),sQuery(id+"F16.wireOp",EDGE,"E95"),sQuery(id+"F16.wireOp",EDGE,"E96")])]});
            var Q5;
            Q5=makeQuery(id+"F17.opExtrude","SWEPT_BODY",BODY,{"disambiguationData":[OSD([sQuery(id+"F16.wireOp",EDGE,"E97"),sQuery(id+"F16.wireOp",EDGE,"E98"),sQuery(id+"F16.wireOp",EDGE,"E99"),sQuery(id+"F16.wireOp",EDGE,"E100")])]});
            var Q6;
            Q6=makeQuery(id+"F17.opExtrude","SWEPT_BODY",BODY,{"disambiguationData":[OSD([sQuery(id+"F16.wireOp",EDGE,"E117"),sQuery(id+"F16.wireOp",EDGE,"E118"),sQuery(id+"F16.wireOp",EDGE,"E119"),sQuery(id+"F16.wireOp",EDGE,"E120")])]});
            var Q7;
            Q7=makeQuery(id+"F17.opExtrude","SWEPT_BODY",BODY,{"disambiguationData":[OSD([sQuery(id+"F16.wireOp",EDGE,"E121"),sQuery(id+"F16.wireOp",EDGE,"E122"),sQuery(id+"F16.wireOp",EDGE,"E123"),sQuery(id+"F16.wireOp",EDGE,"E124"),sQuery(id+"F16.wireOp",EDGE,"E125"),sQuery(id+"F16.wireOp",EDGE,"E126"),sQuery(id+"F16.wireOp",EDGE,"E127"),sQuery(id+"F16.wireOp",EDGE,"E128"),sQuery(id+"F16.wireOp",EDGE,"E129"),sQuery(id+"F16.wireOp",EDGE,"E130"),sQuery(id+"F16.wireOp",EDGE,"E131"),sQuery(id+"F16.wireOp",EDGE,"E132"),sQuery(id+"F16.wireOp",EDGE,"E133"),sQuery(id+"F16.wireOp",EDGE,"E134"),sQuery(id+"F16.wireOp",EDGE,"E135"),sQuery(id+"F16.wireOp",EDGE,"E136"),sQuery(id+"F16.wireOp",EDGE,"E137"),sQuery(id+"F16.wireOp",EDGE,"E138"),sQuery(id+"F16.wireOp",EDGE,"E139"),sQuery(id+"F16.wireOp",EDGE,"E140"),sQuery(id+"F16.wireOp",EDGE,"E141")])]});
            transform(context, id + "F19", {"entities" : qUnion([Q0, Q1, Q2, Q3, Q4, Q5, Q6, Q7]), "transformType" : TransformType.TRANSLATION_3D, "dx" : -6.35 * mm, "dy" : 0 * mm, "dz" : 43.69 * mm, "makeCopy" : false});
        }
        {
            var Q0;
            Q0=makeQuery(id+"F17.opExtrude","SWEPT_BODY",BODY,{"disambiguationData":[OSD([sQuery(id+"F16.wireOp",EDGE,"E27"),sQuery(id+"F16.wireOp",EDGE,"E28"),sQuery(id+"F16.wireOp",EDGE,"E29"),sQuery(id+"F16.wireOp",EDGE,"E30"),sQuery(id+"F16.wireOp",EDGE,"E31"),sQuery(id+"F16.wireOp",EDGE,"E32"),sQuery(id+"F16.wireOp",EDGE,"E33"),sQuery(id+"F16.wireOp",EDGE,"E34"),sQuery(id+"F16.wireOp",EDGE,"E35"),sQuery(id+"F16.wireOp",EDGE,"E36"),sQuery(id+"F16.wireOp",EDGE,"E37"),sQuery(id+"F16.wireOp",EDGE,"E38"),sQuery(id+"F16.wireOp",EDGE,"E39"),sQuery(id+"F16.wireOp",EDGE,"E40"),sQuery(id+"F16.wireOp",EDGE,"E41"),sQuery(id+"F16.wireOp",EDGE,"E42"),sQuery(id+"F16.wireOp",EDGE,"E43"),sQuery(id+"F16.wireOp",EDGE,"E44"),sQuery(id+"F16.wireOp",EDGE,"E45")])]});
            var Q1;
            Q1=makeQuery(id+"F17.opExtrude","SWEPT_BODY",BODY,{"disambiguationData":[OSD([sQuery(id+"F16.wireOp",EDGE,"E46"),sQuery(id+"F16.wireOp",EDGE,"E47"),sQuery(id+"F16.wireOp",EDGE,"E48"),sQuery(id+"F16.wireOp",EDGE,"E49"),sQuery(id+"F16.wireOp",EDGE,"E50"),sQuery(id+"F16.wireOp",EDGE,"E51"),sQuery(id+"F16.wireOp",EDGE,"E52"),sQuery(id+"F16.wireOp",EDGE,"E53")])]});
            var Q2;
            Q2=makeQuery(id+"F17.opExtrude","SWEPT_BODY",BODY,{"disambiguationData":[OSD([sQuery(id+"F16.wireOp",EDGE,"E54"),sQuery(id+"F16.wireOp",EDGE,"E55"),sQuery(id+"F16.wireOp",EDGE,"E56"),sQuery(id+"F16.wireOp",EDGE,"E57"),sQuery(id+"F16.wireOp",EDGE,"E58"),sQuery(id+"F16.wireOp",EDGE,"E59"),sQuery(id+"F16.wireOp",EDGE,"E60"),sQuery(id+"F16.wireOp",EDGE,"E61"),sQuery(id+"F16.wireOp",EDGE,"E62"),sQuery(id+"F16.wireOp",EDGE,"E63"),sQuery(id+"F16.wireOp",EDGE,"E64"),sQuery(id+"F16.wireOp",EDGE,"E65"),sQuery(id+"F16.wireOp",EDGE,"E66"),sQuery(id+"F16.wireOp",EDGE,"E67"),sQuery(id+"F16.wireOp",EDGE,"E68"),sQuery(id+"F16.wireOp",EDGE,"E69"),sQuery(id+"F16.wireOp",EDGE,"E70")])]});
            var Q3;
            Q3=makeQuery(id+"F17.opExtrude","SWEPT_BODY",BODY,{"disambiguationData":[OSD([sQuery(id+"F16.wireOp",EDGE,"E71"),sQuery(id+"F16.wireOp",EDGE,"E72"),sQuery(id+"F16.wireOp",EDGE,"E73"),sQuery(id+"F16.wireOp",EDGE,"E74"),sQuery(id+"F16.wireOp",EDGE,"E75"),sQuery(id+"F16.wireOp",EDGE,"E76"),sQuery(id+"F16.wireOp",EDGE,"E77"),sQuery(id+"F16.wireOp",EDGE,"E78"),sQuery(id+"F16.wireOp",EDGE,"E79"),sQuery(id+"F16.wireOp",EDGE,"E80"),sQuery(id+"F16.wireOp",EDGE,"E81"),sQuery(id+"F16.wireOp",EDGE,"E82"),sQuery(id+"F16.wireOp",EDGE,"E83"),sQuery(id+"F16.wireOp",EDGE,"E84"),sQuery(id+"F16.wireOp",EDGE,"E85"),sQuery(id+"F16.wireOp",EDGE,"E86"),sQuery(id+"F16.wireOp",EDGE,"E87"),sQuery(id+"F16.wireOp",EDGE,"E88"),sQuery(id+"F16.wireOp",EDGE,"E89"),sQuery(id+"F16.wireOp",EDGE,"E90"),sQuery(id+"F16.wireOp",EDGE,"E91"),sQuery(id+"F16.wireOp",EDGE,"E92"),sQuery(id+"F16.wireOp",EDGE,"E142")])]});
            var Q4;
            Q4=makeQuery(id+"F17.opExtrude","SWEPT_BODY",BODY,{"disambiguationData":[OSD([sQuery(id+"F16.wireOp",EDGE,"E93"),sQuery(id+"F16.wireOp",EDGE,"E94"),sQuery(id+"F16.wireOp",EDGE,"E95"),sQuery(id+"F16.wireOp",EDGE,"E96")])]});
            var Q5;
            Q5=makeQuery(id+"F17.opExtrude","SWEPT_BODY",BODY,{"disambiguationData":[OSD([sQuery(id+"F16.wireOp",EDGE,"E97"),sQuery(id+"F16.wireOp",EDGE,"E98"),sQuery(id+"F16.wireOp",EDGE,"E99"),sQuery(id+"F16.wireOp",EDGE,"E100")])]});
            var Q6;
            Q6=makeQuery(id+"F17.opExtrude","SWEPT_BODY",BODY,{"disambiguationData":[OSD([sQuery(id+"F16.wireOp",EDGE,"E117"),sQuery(id+"F16.wireOp",EDGE,"E118"),sQuery(id+"F16.wireOp",EDGE,"E119"),sQuery(id+"F16.wireOp",EDGE,"E120")])]});
            var Q7;
            Q7=makeQuery(id+"F17.opExtrude","SWEPT_BODY",BODY,{"disambiguationData":[OSD([sQuery(id+"F16.wireOp",EDGE,"E121"),sQuery(id+"F16.wireOp",EDGE,"E122"),sQuery(id+"F16.wireOp",EDGE,"E123"),sQuery(id+"F16.wireOp",EDGE,"E124"),sQuery(id+"F16.wireOp",EDGE,"E125"),sQuery(id+"F16.wireOp",EDGE,"E126"),sQuery(id+"F16.wireOp",EDGE,"E127"),sQuery(id+"F16.wireOp",EDGE,"E128"),sQuery(id+"F16.wireOp",EDGE,"E129"),sQuery(id+"F16.wireOp",EDGE,"E130"),sQuery(id+"F16.wireOp",EDGE,"E131"),sQuery(id+"F16.wireOp",EDGE,"E132"),sQuery(id+"F16.wireOp",EDGE,"E133"),sQuery(id+"F16.wireOp",EDGE,"E134"),sQuery(id+"F16.wireOp",EDGE,"E135"),sQuery(id+"F16.wireOp",EDGE,"E136"),sQuery(id+"F16.wireOp",EDGE,"E137"),sQuery(id+"F16.wireOp",EDGE,"E138"),sQuery(id+"F16.wireOp",EDGE,"E139"),sQuery(id+"F16.wireOp",EDGE,"E140"),sQuery(id+"F16.wireOp",EDGE,"E141")])]});
            var Q8;
            Q8=makeQuery(id+"F3.opExtrude","SWEPT_BODY",BODY,{"disambiguationData":[OSD([sQuery(id+"F0.wireOp",EDGE,"E0.bottom"),sQuery(id+"F0.wireOp",EDGE,"E1.1"),sQuery(id+"F0.wireOp",EDGE,"E1.2"),sQuery(id+"F0.wireOp",EDGE,"E3"),sQuery(id+"F0.wireOp",EDGE,"E4")])]});
            booleanBodies(context, id + "F20", {"operationType" : BooleanOperationType.SUBTRACTION, "tools" : qUnion([Q0, Q1, Q2, Q3, Q4, Q5, Q6, Q7]), "targets" : qUnion([Q8]), "keepTools" : true});
        }
    });
